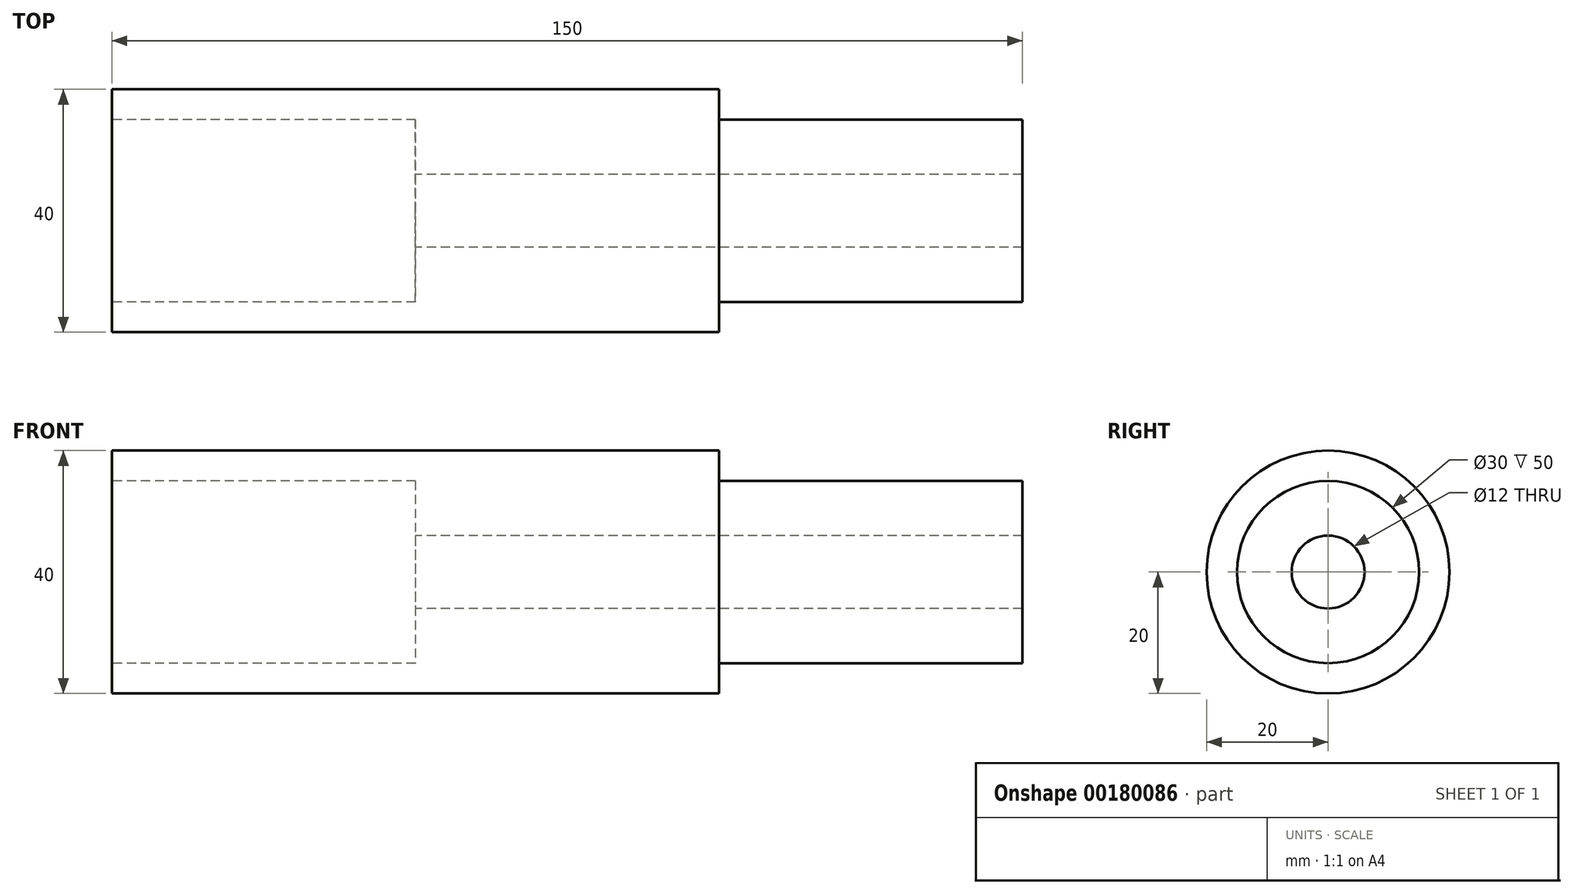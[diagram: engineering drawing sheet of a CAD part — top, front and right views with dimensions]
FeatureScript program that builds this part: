
annotation { "Feature Type Name" : "Feature", "Feature Type Description" : "" }
export const myFeature = defineFeature(function(context is Context, id is Id, definition is map)
    precondition{}
    {
        {
            var Q0;
            Q0=qCreatedBy(makeId("Right.planeOp"),FACE);
            var sketch = newSketch(context, id + "F0", { "sketchPlane" : qUnion([Q0])});
            skCircle(sketch, "E0", {"center": v(0, 0) * mm, "radius": 20 * mm});
            skSolve(sketch);
        }
        {
            var Q0;
            Q0=makeQuery(id+"F0.imprint","IMPRINT",FACE,{"disambiguationData":[TD([[makeQuery(id+"F0.imprint","IMPRINT",EDGE,{"derivedFrom":sQuery(id+"F0.wireOp",EDGE,"E0")}),1.0]])]});
            extrude(context, id + "F1", {"entities" : qUnion([Q0]), "depth" : 150 * mm});
        }
        {
            var Q0;
            Q0=makeQuery(id+"F1.opExtrude","CAP_FACE",FACE,{"disambiguationData":[OSD([sQuery(id+"F0.wireOp",EDGE,"E0")])],"isStart":true});
            var sketch = newSketch(context, id + "F2", { "sketchPlane" : qUnion([Q0])});
            skCircle(sketch, "E1", {"center": v(0, 0) * mm, "radius": 15 * mm});
            skCircle(sketch, "E2", {"center": v(0, 0) * mm, "radius": 6 * mm});
            skSolve(sketch);
        }
        {
            var Q0;
            Q0=makeQuery(id+"F2.imprint","IMPRINT",FACE,{"disambiguationData":[TD([[makeQuery(id+"F2.imprint","IMPRINT",EDGE,{"derivedFrom":sQuery(id+"F2.wireOp",EDGE,"E1")}),1.0]])]});
            extrude(context, id + "F3", {"entities" : qUnion([Q0]), "operationType" : NewBodyOperationType.REMOVE, "oppositeDirection" : true, "depth" : 50 * mm});
        }
        {
            var Q0;
            Q0=makeQuery(id+"F3.boolean.opBoolean","SPLIT",FACE,{"disambiguationData":[TD([makeQuery(id+"F3.opExtrude","SWEPT_FACE",FACE,{"disambiguationData":[OSD([sQuery(id+"F2.wireOp",EDGE,"E2")])]})])],"derivedFrom":makeQuery(id+"F1.opExtrude","CAP_FACE",FACE,{"disambiguationData":[OSD([sQuery(id+"F0.wireOp",EDGE,"E0")])],"isStart":true})});
            extrude(context, id + "F4", {"entities" : qUnion([Q0]), "operationType" : NewBodyOperationType.REMOVE, "oppositeDirection" : true, "depth" : 150 * mm});
        }
        {
            var Q0;
            Q0=makeQuery(id+"F1.opExtrude","CAP_FACE",FACE,{"disambiguationData":[OSD([sQuery(id+"F0.wireOp",EDGE,"E0")])],"isStart":false});
            var sketch = newSketch(context, id + "F5", { "sketchPlane" : qUnion([Q0])});
            skCircle(sketch, "E3", {"center": v(0, 0) * mm, "radius": 15 * mm});
            skSolve(sketch);
        }
        {
            var Q0;
            Q0=makeQuery(id+"F5.imprint","IMPRINT",FACE,{"disambiguationData":[TD([[makeQuery(id+"F5.imprint","IMPRINT",EDGE,{"derivedFrom":sQuery(id+"F5.wireOp",EDGE,"E3")}),-1.0]])]});
            extrude(context, id + "F6", {"entities" : qUnion([Q0]), "operationType" : NewBodyOperationType.REMOVE, "oppositeDirection" : true, "depth" : 50 * mm});
        }
    });
